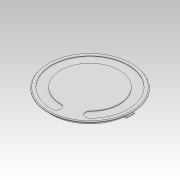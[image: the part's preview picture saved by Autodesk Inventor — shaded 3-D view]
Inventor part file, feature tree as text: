
AUTODESK INVENTOR PART (.ipt)
format: ipt  version: 2020 (Build 240168000, 168)  size: 202,752 bytes
history: native  units: mm
features: other x3, sketch x3, extrude x2, fillet x2, revolve x1, projected_geometry x1
ambient origin geometry x8: Origin, YZ Plane, XZ Plane, XY Plane, X Axis, Y Axis, Z Axis, Center Point
bodies: Solid1 (feature_tree)
feature tree (12):
  other  "Blocks"
  revolve  "Revolution1"  [1 undecoded]
  extrude  "Extrusion1"  Depth=1.0mm
  fillet  "Fillet1"  [1 undecoded]
  extrude  "Extrusion2"  Depth=0.7mm
  fillet  "Fillet2"  Radius=2.0mm
  sketch  "Sketch1"  dims[d0=37.35mm d1=3.0mm]
  sketch  "Sketch2"  dims[d2=1.0mm d3=1.4mm d4=120.0deg]
  projected_geometry  "Projected Loop1"
  sketch  "Sketch3"  dims[d5=2.0mm d6=2.0mm d7=2.0mm d8=0.5mm d9=90.0deg d10=8.0mm d11=1.0mm d12=0.0mm d13=1.0mm d14=8.0mm d15=0.4mm d16=0.0mm d17=0.7mm]
  other  "Block1"
  other  "Block1:1"
note: 2 required parameter values undecoded (feature->parameter linkage not recoverable at this tier; creation-order binding heuristic only, values carry confidence <= 0.55)